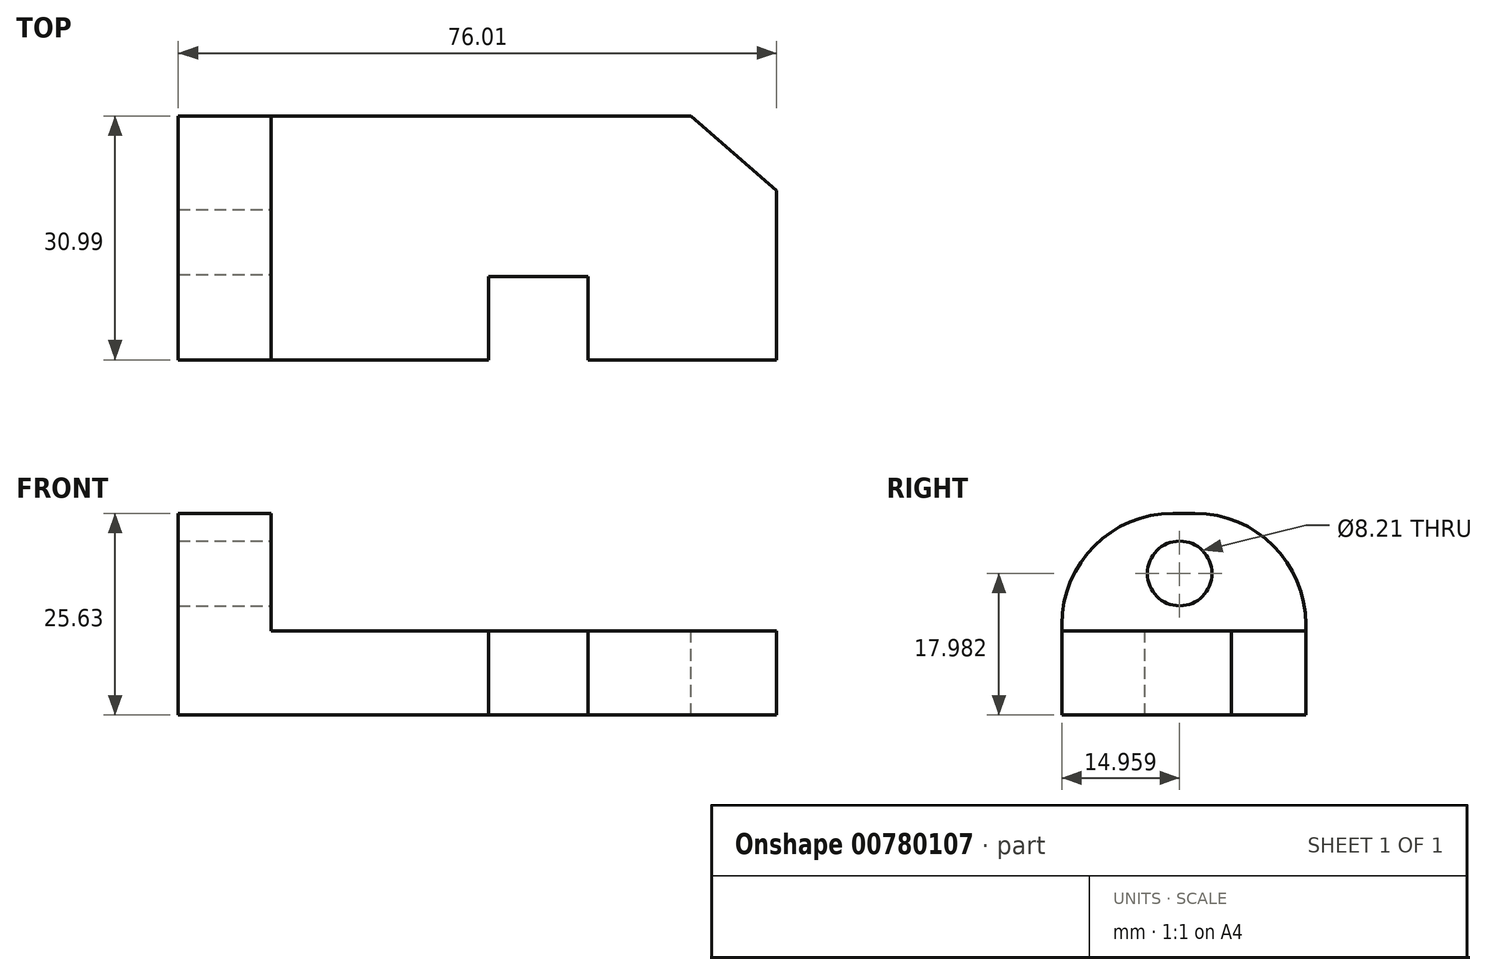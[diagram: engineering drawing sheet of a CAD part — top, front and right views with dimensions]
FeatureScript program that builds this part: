
annotation { "Feature Type Name" : "Feature", "Feature Type Description" : "" }
export const myFeature = defineFeature(function(context is Context, id is Id, definition is map)
    precondition{}
    {
        {
            var Q0;
            Q0=qCreatedBy(makeId("Front.planeOp"),FACE);
            var sketch = newSketch(context, id + "F0", { "sketchPlane" : qUnion([Q0])});
            skLineSegment(sketch, "E0", {"start": v(0, 0) * mm, "end": v(0, -25.63) * mm});
            skLineSegment(sketch, "E1", {"start": v(0, -25.63) * mm, "end": v(76.01, -25.63) * mm});
            skLineSegment(sketch, "E2", {"start": v(76.01, -25.63) * mm, "end": v(76.01, -14.94) * mm});
            skLineSegment(sketch, "E3", {"start": v(76.01, -14.94) * mm, "end": v(11.81, -14.94) * mm});
            skLineSegment(sketch, "E4", {"start": v(11.81, -14.94) * mm, "end": v(11.81, 0) * mm});
            skLineSegment(sketch, "E5", {"start": v(11.81, 0) * mm, "end": v(0, 0) * mm});
            skSolve(sketch);
        }
        {
            var Q0;
            Q0=makeQuery(id+"F0.imprint","IMPRINT",FACE,{"disambiguationData":[TD([[makeQuery(id+"F0.imprint","IMPRINT",EDGE,{"derivedFrom":sQuery(id+"F0.wireOp",EDGE,"E0")}),1.0]])]});
            extrude(context, id + "F1", {"entities" : qUnion([Q0]), "depth" : 30.99 * mm, "offsetDistance" : 25.4 * mm});
        }
        {
            var Q0;
            Q0=makeQuery(id+"F1.opExtrude","SWEPT_FACE",FACE,{"disambiguationData":[OSD([sQuery(id+"F0.wireOp",EDGE,"E3")])]});
            var sketch = newSketch(context, id + "F2", { "sketchPlane" : qUnion([Q0])});
            skLineSegment(sketch, "E6", {"start": v(65.15, 0) * mm, "end": v(76.01, -9.49) * mm});
            skLineSegment(sketch, "E7", {"start": v(52.08, -30.99) * mm, "end": v(52.08, -20.43) * mm});
            skLineSegment(sketch, "E8", {"start": v(52.08, -20.43) * mm, "end": v(39.4, -20.43) * mm});
            skLineSegment(sketch, "E9", {"start": v(39.4, -20.43) * mm, "end": v(39.4, -30.99) * mm});
            skSolve(sketch);
        }
        {
            var Q0;
            {var subQ0=sQuery(id+"F2.wireOp",EDGE,"E7");Q0=makeQuery(id+"F2.imprint","IMPRINT",FACE,{"disambiguationData":[TD([[makeQuery(id+"F2.imprint","IMPRINT",EDGE,{"derivedFrom":subQ0}),1.0]])]});}
            extrude(context, id + "F3", {"entities" : qUnion([Q0]), "operationType" : NewBodyOperationType.REMOVE, "oppositeDirection" : true, "depth" : 25.4 * mm, "offsetDistance" : 25.4 * mm});
        }
        {
            var Q0;
            {var subQ0=sQuery(id+"F2.wireOp",EDGE,"E6");Q0=makeQuery(id+"F2.imprint","IMPRINT",FACE,{"disambiguationData":[TD([[makeQuery(id+"F2.imprint","IMPRINT",EDGE,{"derivedFrom":subQ0}),1.0]])]});}
            var Q1;
            {var subQ0=sQuery(id+"F2.wireOp",EDGE,"E7");Q1=makeQuery(id+"F2.imprint","IMPRINT",FACE,{"disambiguationData":[TD([[makeQuery(id+"F2.imprint","IMPRINT",EDGE,{"derivedFrom":subQ0}),1.0]])]});}
            extrude(context, id + "F4", {"entities" : qUnion([Q0, Q1]), "operationType" : NewBodyOperationType.REMOVE, "oppositeDirection" : true, "depth" : 25.4 * mm, "offsetDistance" : 25.4 * mm});
        }
        {
            var Q0;
            Q0=makeQuery(id+"F1.opExtrude","SWEPT_FACE",FACE,{"disambiguationData":[OSD([sQuery(id+"F0.wireOp",EDGE,"E4")])]});
            var sketch = newSketch(context, id + "F5", { "sketchPlane" : qUnion([Q0])});
            skCircle(sketch, "E10", {"center": v(-16.03, -7.65) * mm, "radius": 4.1 * mm});
            skSolve(sketch);
        }
        {
            var Q0;
            Q0=makeQuery(id+"F5.imprint","IMPRINT",FACE,{"disambiguationData":[TD([[makeQuery(id+"F5.imprint","IMPRINT",EDGE,{"derivedFrom":sQuery(id+"F5.wireOp",EDGE,"E10")}),1.0]])]});
            extrude(context, id + "F6", {"entities" : qUnion([Q0]), "operationType" : NewBodyOperationType.REMOVE, "oppositeDirection" : true, "depth" : 25.4 * mm, "offsetDistance" : 25.4 * mm});
        }
        {
            var Q0;
            Q0=makeQuery(id+"F1.opExtrude","CAP_EDGE",EDGE,{"disambiguationData":[OSD([sQuery(id+"F0.wireOp",EDGE,"E5")])],"isStart":false});
            var Q1;
            Q1=makeQuery(id+"F1.opExtrude","CAP_EDGE",EDGE,{"disambiguationData":[OSD([sQuery(id+"F0.wireOp",EDGE,"E5")])],"isStart":true});
            fillet(context, id + "F7", {"entities" : qUnion([Q0, Q1]), "radius" : 14.1 * mm, "tangentPropagation" : true, "allowEdgeOverflow" : false});
        }
    });
